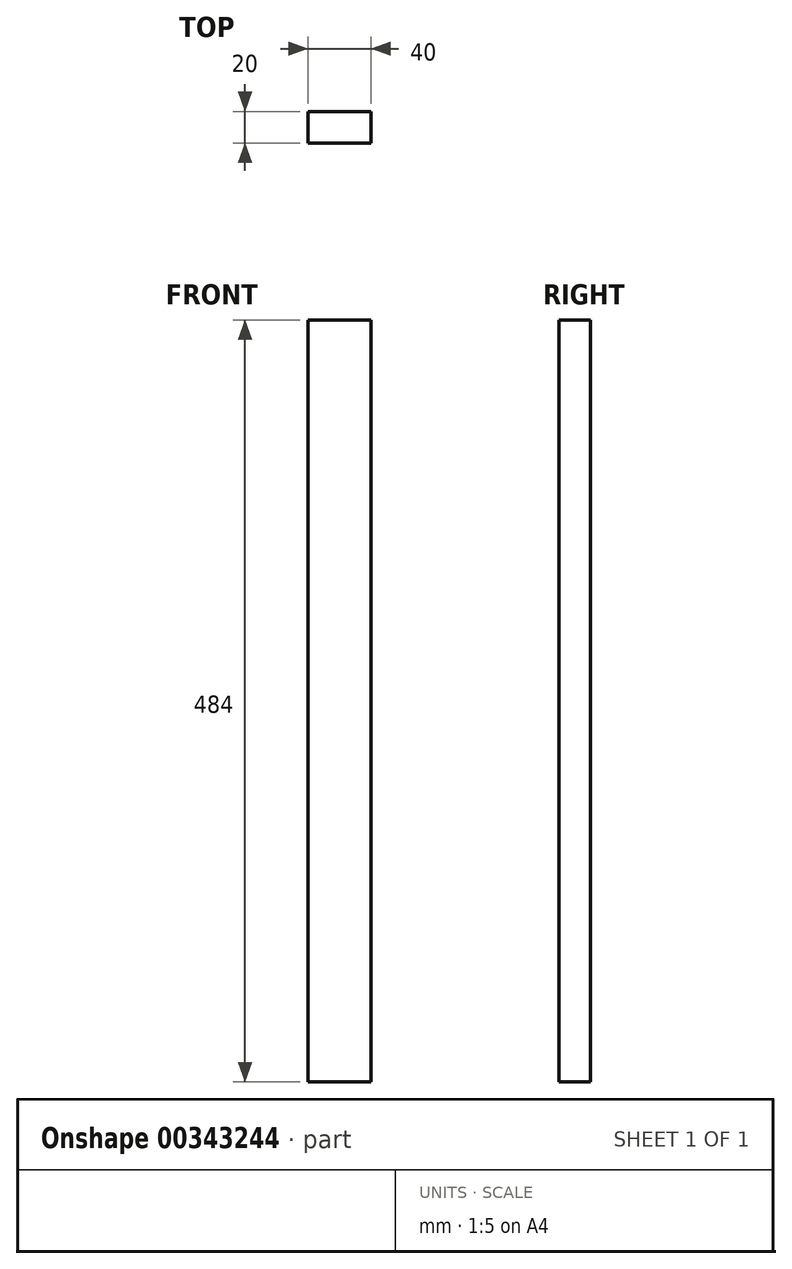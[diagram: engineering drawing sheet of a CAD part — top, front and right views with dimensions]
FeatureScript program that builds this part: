
annotation { "Feature Type Name" : "Feature", "Feature Type Description" : "" }
export const myFeature = defineFeature(function(context is Context, id is Id, definition is map)
    precondition{}
    {
        {
            var Q0;
            Q0=qCreatedBy(makeId("Front.planeOp"),FACE);
            var sketch = newSketch(context, id + "F0", { "sketchPlane" : qUnion([Q0])});
            skLineSegment(sketch, "E0.bottom", {"start": v(20, 242) * mm, "end": v(-20, 242) * mm});
            skLineSegment(sketch, "E0.top", {"start": v(20, -242) * mm, "end": v(-20, -242) * mm});
            skLineSegment(sketch, "E0.left", {"start": v(20, 242) * mm, "end": v(20, -242) * mm});
            skLineSegment(sketch, "E0.right", {"start": v(-20, 242) * mm, "end": v(-20, -242) * mm});
            skPoint(sketch, "E0.middle", {"position": v(0, 0) * mm});
            skSolve(sketch);
        }
        {
            var Q0;
            Q0=makeQuery(id+"F0.imprint","IMPRINT",FACE,{"disambiguationData":[TD([[makeQuery(id+"F0.imprint","IMPRINT",EDGE,{"derivedFrom":sQuery(id+"F0.wireOp",EDGE,"E0.bottom")}),1.0]])]});
            extrude(context, id + "F1", {"entities" : qUnion([Q0]), "depth" : 20 * mm});
        }
    });
